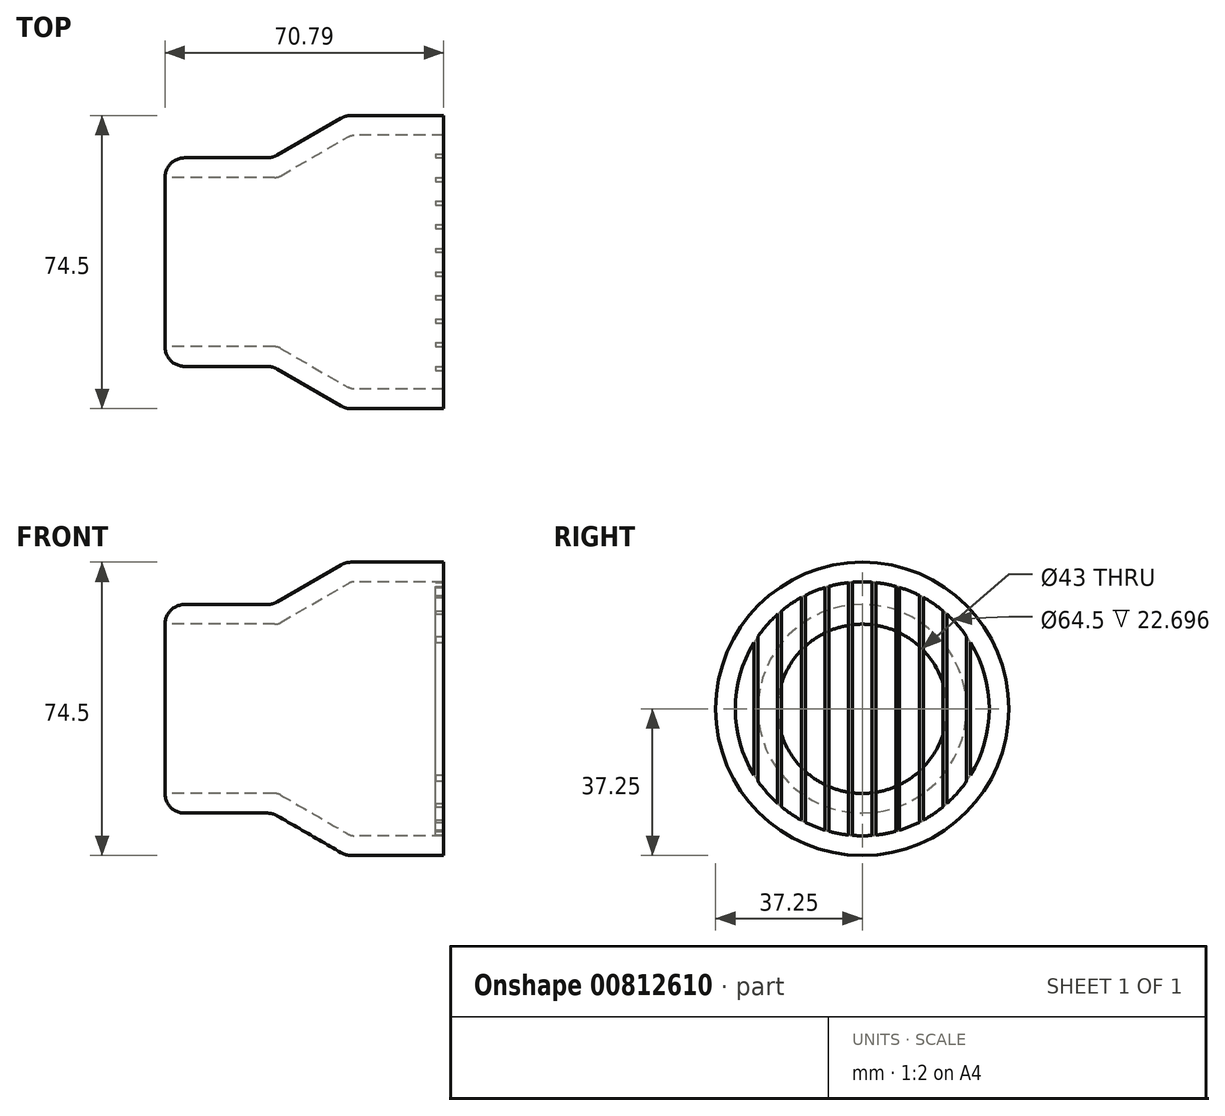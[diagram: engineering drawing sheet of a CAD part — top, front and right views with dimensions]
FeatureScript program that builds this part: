
annotation { "Feature Type Name" : "Feature", "Feature Type Description" : "" }
export const myFeature = defineFeature(function(context is Context, id is Id, definition is map)
    precondition{}
    {
        {
            var Q0;
            Q0=qCreatedBy(makeId("Top.planeOp"),FACE);
            var sketch = newSketch(context, id + "F0", { "sketchPlane" : qUnion([Q0])});
            skLineSegment(sketch, "E0", {"start": v(-28.67, 21.5) * mm, "end": v(0, 21.5) * mm});
            skLineSegment(sketch, "E1", {"start": v(0, 21.5) * mm, "end": v(18.62, 32.25) * mm});
            skLineSegment(sketch, "E2", {"start": v(18.62, 32.25) * mm, "end": v(40.12, 32.25) * mm});
            skLineSegment(sketch, "E3.0", {"start": v(17.28, 37.25) * mm, "end": v(40.12, 37.25) * mm});
            skLineSegment(sketch, "E3.1", {"start": v(-1.34, 26.5) * mm, "end": v(17.28, 37.25) * mm});
            skLineSegment(sketch, "E3.2", {"start": v(-28.67, 26.5) * mm, "end": v(-1.34, 26.5) * mm});
            skLineSegment(sketch, "E4", {"start": v(-28.67, 21.5) * mm, "end": v(-28.67, 26.5) * mm});
            skLineSegment(sketch, "E5", {"start": v(40.12, 37.25) * mm, "end": v(40.12, 32.25) * mm});
            skLineSegment(sketch, "E6", {"start": v(-63.57, 0) * mm, "end": v(46.05, 0) * mm});
            skSolve(sketch);
        }
        {
            var Q0;
            Q0=qSketchRegion(id+"F0",true);
            var Q1;
            Q1=sQuery(id+"F0.wireOp",EDGE,"E6");
            revolve(context, id + "F1", {"surfaceOperationType" : NewSurfaceOperationType.NEW, "entities" : qUnion([Q0]), "axis" : qUnion([Q1]), "revolveType" : RevolveType.FULL});
        }
        {
            var Q0;
            Q0=makeQuery(id+"F1.opRevolve","SWEPT_FACE",FACE,{"disambiguationData":[OSD([sQuery(id+"F0.wireOp",EDGE,"E5")])]});
            var sketch = newSketch(context, id + "F2", { "sketchPlane" : qUnion([Q0])});
            skCircle(sketch, "E7.0", {"center": v(0, 0) * mm, "radius": 37.25 * mm});
            skSolve(sketch);
        }
        {
            var Q0;
            Q0=qSketchRegion(id+"F2",true);
            extrude(context, id + "F3", {"entities" : qUnion([Q0]), "operationType" : NewBodyOperationType.ADD, "depth" : 2 * mm, "offsetDistance" : 25 * mm});
        }
        {
            var Q0;
            Q0=makeQuery(id+"F3.opExtrude","CAP_FACE",FACE,{"disambiguationData":[OSD([sQuery(id+"F2.wireOp",EDGE,"E7.0")])],"isStart":false});
            var sketch = newSketch(context, id + "F4", { "sketchPlane" : qUnion([Q0])});
            skLineSegment(sketch, "E8.bottom", {"start": v(-2.5, 42.44) * mm, "end": v(2.5, 42.44) * mm});
            skLineSegment(sketch, "E8.top", {"start": v(-2.5, -43.56) * mm, "end": v(2.5, -43.56) * mm});
            skLineSegment(sketch, "E8.left", {"start": v(-2.5, 42.44) * mm, "end": v(-2.5, -43.56) * mm});
            skLineSegment(sketch, "E8.right", {"start": v(2.5, 42.44) * mm, "end": v(2.5, -43.56) * mm});
            skLineSegment(sketch, "E9.1.0.0", {"start": v(3.5, -43.56) * mm, "end": v(8.5, -43.56) * mm});
            skLineSegment(sketch, "E9.1.0.1", {"start": v(8.5, 42.44) * mm, "end": v(8.5, -43.56) * mm});
            skLineSegment(sketch, "E9.1.0.2", {"start": v(3.5, 42.44) * mm, "end": v(3.5, -43.56) * mm});
            skLineSegment(sketch, "E9.1.0.3", {"start": v(3.5, 42.44) * mm, "end": v(8.5, 42.44) * mm});
            skLineSegment(sketch, "E9.2.0.0", {"start": v(9.5, -43.56) * mm, "end": v(14.5, -43.56) * mm});
            skLineSegment(sketch, "E9.2.0.1", {"start": v(14.5, 42.44) * mm, "end": v(14.5, -43.56) * mm});
            skLineSegment(sketch, "E9.2.0.2", {"start": v(9.5, 42.44) * mm, "end": v(9.5, -43.56) * mm});
            skLineSegment(sketch, "E9.2.0.3", {"start": v(9.5, 42.44) * mm, "end": v(14.5, 42.44) * mm});
            skLineSegment(sketch, "E9.3.0.0", {"start": v(15.5, -43.56) * mm, "end": v(20.5, -43.56) * mm});
            skLineSegment(sketch, "E9.3.0.1", {"start": v(20.5, 42.44) * mm, "end": v(20.5, -43.56) * mm});
            skLineSegment(sketch, "E9.3.0.2", {"start": v(15.5, 42.44) * mm, "end": v(15.5, -43.56) * mm});
            skLineSegment(sketch, "E9.3.0.3", {"start": v(15.5, 42.44) * mm, "end": v(20.5, 42.44) * mm});
            skLineSegment(sketch, "E9.4.0.0", {"start": v(21.5, -43.56) * mm, "end": v(26.5, -43.56) * mm});
            skLineSegment(sketch, "E9.4.0.1", {"start": v(26.5, 42.44) * mm, "end": v(26.5, -43.56) * mm});
            skLineSegment(sketch, "E9.4.0.2", {"start": v(21.5, 42.44) * mm, "end": v(21.5, -43.56) * mm});
            skLineSegment(sketch, "E9.4.0.3", {"start": v(21.5, 42.44) * mm, "end": v(26.5, 42.44) * mm});
            skLineSegment(sketch, "E9.5.0.0", {"start": v(27.5, -43.56) * mm, "end": v(32.5, -43.56) * mm});
            skLineSegment(sketch, "E9.5.0.1", {"start": v(32.5, 42.44) * mm, "end": v(32.5, -43.56) * mm});
            skLineSegment(sketch, "E9.5.0.2", {"start": v(27.5, 42.44) * mm, "end": v(27.5, -43.56) * mm});
            skLineSegment(sketch, "E9.5.0.3", {"start": v(27.5, 42.44) * mm, "end": v(32.5, 42.44) * mm});
            skLineSegment(sketch, "E9.direction1", {"start": v(-2.5, -43.56) * mm, "end": v(3.5, -43.56) * mm, "construction": true});
            skLineSegment(sketch, "E10.1.0.0", {"start": v(-3.5, 42.44) * mm, "end": v(-3.5, -43.56) * mm});
            skLineSegment(sketch, "E10.1.0.1", {"start": v(-8.5, -43.56) * mm, "end": v(-3.5, -43.56) * mm});
            skLineSegment(sketch, "E10.1.0.2", {"start": v(-8.5, 42.44) * mm, "end": v(-8.5, -43.56) * mm});
            skLineSegment(sketch, "E10.1.0.3", {"start": v(-8.5, 42.44) * mm, "end": v(-3.5, 42.44) * mm});
            skLineSegment(sketch, "E10.2.0.0", {"start": v(-9.5, 42.44) * mm, "end": v(-9.5, -43.56) * mm});
            skLineSegment(sketch, "E10.2.0.1", {"start": v(-14.5, -43.56) * mm, "end": v(-9.5, -43.56) * mm});
            skLineSegment(sketch, "E10.2.0.2", {"start": v(-14.5, 42.44) * mm, "end": v(-14.5, -43.56) * mm});
            skLineSegment(sketch, "E10.2.0.3", {"start": v(-14.5, 42.44) * mm, "end": v(-9.5, 42.44) * mm});
            skLineSegment(sketch, "E10.3.0.0", {"start": v(-15.5, 42.44) * mm, "end": v(-15.5, -43.56) * mm});
            skLineSegment(sketch, "E10.3.0.1", {"start": v(-20.5, -43.56) * mm, "end": v(-15.5, -43.56) * mm});
            skLineSegment(sketch, "E10.3.0.2", {"start": v(-20.5, 42.44) * mm, "end": v(-20.5, -43.56) * mm});
            skLineSegment(sketch, "E10.3.0.3", {"start": v(-20.5, 42.44) * mm, "end": v(-15.5, 42.44) * mm});
            skLineSegment(sketch, "E10.4.0.0", {"start": v(-21.5, 42.44) * mm, "end": v(-21.5, -43.56) * mm});
            skLineSegment(sketch, "E10.4.0.1", {"start": v(-26.5, -43.56) * mm, "end": v(-21.5, -43.56) * mm});
            skLineSegment(sketch, "E10.4.0.2", {"start": v(-26.5, 42.44) * mm, "end": v(-26.5, -43.56) * mm});
            skLineSegment(sketch, "E10.4.0.3", {"start": v(-26.5, 42.44) * mm, "end": v(-21.5, 42.44) * mm});
            skLineSegment(sketch, "E10.5.0.0", {"start": v(-27.5, 42.44) * mm, "end": v(-27.5, -43.56) * mm});
            skLineSegment(sketch, "E10.5.0.1", {"start": v(-32.5, -43.56) * mm, "end": v(-27.5, -43.56) * mm});
            skLineSegment(sketch, "E10.5.0.2", {"start": v(-32.5, 42.44) * mm, "end": v(-32.5, -43.56) * mm});
            skLineSegment(sketch, "E10.5.0.3", {"start": v(-32.5, 42.44) * mm, "end": v(-27.5, 42.44) * mm});
            skLineSegment(sketch, "E10.direction1", {"start": v(-2.5, -43.56) * mm, "end": v(-8.5, -43.56) * mm, "construction": true});
            skCircle(sketch, "E11.0", {"center": v(0, 0) * mm, "radius": 37.25 * mm});
            skCircle(sketch, "E12", {"center": v(0, 0) * mm, "radius": 32.25 * mm});
            skSolve(sketch);
        }
        {
            var Q0;
            {var subQ0=sQuery(id+"F4.wireOp",EDGE,"E12");var subQ1=sQuery(id+"F4.wireOp",EDGE,"E9.5.0.2");var subQ2=makeQuery(id+"F4.imprint","INTERSECT",VERTEX,{"disambiguationData":[OD(0.0)],"derivedFrom":[subQ1,subQ0]});Q0=makeQuery(id+"F4.imprint","IMPRINT",FACE,{"disambiguationData":[TD([[makeQuery(id+"F4.imprint","IMPRINT",EDGE,{"disambiguationData":[TD([[subQ2,-1.0]])],"derivedFrom":subQ1}),1.0]])]});}
            var Q1;
            {var subQ0=sQuery(id+"F4.wireOp",EDGE,"E12");var subQ1=sQuery(id+"F4.wireOp",EDGE,"E9.4.0.1");var subQ2=makeQuery(id+"F4.imprint","INTERSECT",VERTEX,{"disambiguationData":[OD(0.0)],"derivedFrom":[subQ1,subQ0]});Q1=makeQuery(id+"F4.imprint","IMPRINT",FACE,{"disambiguationData":[TD([[makeQuery(id+"F4.imprint","IMPRINT",EDGE,{"disambiguationData":[TD([[subQ2,-1.0]])],"derivedFrom":subQ1}),-1.0]])]});}
            var Q2;
            {var subQ0=sQuery(id+"F4.wireOp",EDGE,"E12");var subQ1=sQuery(id+"F4.wireOp",EDGE,"E9.3.0.1");var subQ2=makeQuery(id+"F4.imprint","INTERSECT",VERTEX,{"disambiguationData":[OD(0.0)],"derivedFrom":[subQ1,subQ0]});Q2=makeQuery(id+"F4.imprint","IMPRINT",FACE,{"disambiguationData":[TD([[makeQuery(id+"F4.imprint","IMPRINT",EDGE,{"disambiguationData":[TD([[subQ2,-1.0]])],"derivedFrom":subQ1}),-1.0]])]});}
            var Q3;
            {var subQ0=sQuery(id+"F4.wireOp",EDGE,"E12");var subQ1=sQuery(id+"F4.wireOp",EDGE,"E9.2.0.1");var subQ2=makeQuery(id+"F4.imprint","INTERSECT",VERTEX,{"disambiguationData":[OD(0.0)],"derivedFrom":[subQ1,subQ0]});Q3=makeQuery(id+"F4.imprint","IMPRINT",FACE,{"disambiguationData":[TD([[makeQuery(id+"F4.imprint","IMPRINT",EDGE,{"disambiguationData":[TD([[subQ2,-1.0]])],"derivedFrom":subQ1}),-1.0]])]});}
            var Q4;
            {var subQ0=sQuery(id+"F4.wireOp",EDGE,"E12");var subQ1=sQuery(id+"F4.wireOp",EDGE,"E9.1.0.1");var subQ2=makeQuery(id+"F4.imprint","INTERSECT",VERTEX,{"disambiguationData":[OD(0.0)],"derivedFrom":[subQ1,subQ0]});Q4=makeQuery(id+"F4.imprint","IMPRINT",FACE,{"disambiguationData":[TD([[makeQuery(id+"F4.imprint","IMPRINT",EDGE,{"disambiguationData":[TD([[subQ2,-1.0]])],"derivedFrom":subQ1}),-1.0]])]});}
            var Q5;
            {var subQ0=sQuery(id+"F4.wireOp",EDGE,"E12");var subQ1=sQuery(id+"F4.wireOp",EDGE,"E8.left");var subQ2=makeQuery(id+"F4.imprint","INTERSECT",VERTEX,{"disambiguationData":[OD(0.0)],"derivedFrom":[subQ1,subQ0]});Q5=makeQuery(id+"F4.imprint","IMPRINT",FACE,{"disambiguationData":[TD([[makeQuery(id+"F4.imprint","IMPRINT",EDGE,{"disambiguationData":[TD([[subQ2,-1.0]])],"derivedFrom":subQ1}),1.0]])]});}
            var Q6;
            {var subQ0=sQuery(id+"F4.wireOp",EDGE,"E12");var subQ1=sQuery(id+"F4.wireOp",EDGE,"E10.1.0.0");var subQ2=makeQuery(id+"F4.imprint","INTERSECT",VERTEX,{"disambiguationData":[OD(0.0)],"derivedFrom":[subQ1,subQ0]});Q6=makeQuery(id+"F4.imprint","IMPRINT",FACE,{"disambiguationData":[TD([[makeQuery(id+"F4.imprint","IMPRINT",EDGE,{"disambiguationData":[TD([[subQ2,-1.0]])],"derivedFrom":subQ1}),-1.0]])]});}
            var Q7;
            {var subQ0=sQuery(id+"F4.wireOp",EDGE,"E12");var subQ1=sQuery(id+"F4.wireOp",EDGE,"E10.2.0.0");var subQ2=makeQuery(id+"F4.imprint","INTERSECT",VERTEX,{"disambiguationData":[OD(0.0)],"derivedFrom":[subQ1,subQ0]});Q7=makeQuery(id+"F4.imprint","IMPRINT",FACE,{"disambiguationData":[TD([[makeQuery(id+"F4.imprint","IMPRINT",EDGE,{"disambiguationData":[TD([[subQ2,-1.0]])],"derivedFrom":subQ1}),-1.0]])]});}
            var Q8;
            {var subQ0=sQuery(id+"F4.wireOp",EDGE,"E12");var subQ1=sQuery(id+"F4.wireOp",EDGE,"E10.3.0.0");var subQ2=makeQuery(id+"F4.imprint","INTERSECT",VERTEX,{"disambiguationData":[OD(0.0)],"derivedFrom":[subQ1,subQ0]});Q8=makeQuery(id+"F4.imprint","IMPRINT",FACE,{"disambiguationData":[TD([[makeQuery(id+"F4.imprint","IMPRINT",EDGE,{"disambiguationData":[TD([[subQ2,-1.0]])],"derivedFrom":subQ1}),-1.0]])]});}
            var Q9;
            {var subQ0=sQuery(id+"F4.wireOp",EDGE,"E12");var subQ1=sQuery(id+"F4.wireOp",EDGE,"E10.4.0.0");var subQ2=makeQuery(id+"F4.imprint","INTERSECT",VERTEX,{"disambiguationData":[OD(0.0)],"derivedFrom":[subQ1,subQ0]});Q9=makeQuery(id+"F4.imprint","IMPRINT",FACE,{"disambiguationData":[TD([[makeQuery(id+"F4.imprint","IMPRINT",EDGE,{"disambiguationData":[TD([[subQ2,-1.0]])],"derivedFrom":subQ1}),-1.0]])]});}
            var Q10;
            {var subQ0=sQuery(id+"F4.wireOp",EDGE,"E12");var subQ1=sQuery(id+"F4.wireOp",EDGE,"E10.5.0.0");var subQ2=makeQuery(id+"F4.imprint","INTERSECT",VERTEX,{"disambiguationData":[OD(0.0)],"derivedFrom":[subQ1,subQ0]});Q10=makeQuery(id+"F4.imprint","IMPRINT",FACE,{"disambiguationData":[TD([[makeQuery(id+"F4.imprint","IMPRINT",EDGE,{"disambiguationData":[TD([[subQ2,-1.0]])],"derivedFrom":subQ1}),-1.0]])]});}
            var Q11;
            Q11=makeQuery(id+"F3.opExtrude","CAP_FACE",FACE,{"disambiguationData":[OSD([sQuery(id+"F2.wireOp",EDGE,"E7.0")])],"isStart":true});
            extrude(context, id + "F5", {"entities" : qUnion([Q0, Q1, Q2, Q3, Q4, Q5, Q6, Q7, Q8, Q9, Q10]), "operationType" : NewBodyOperationType.REMOVE, "endBound" : BoundingType.UP_TO_SURFACE, "oppositeDirection" : true, "depth" : 25 * mm, "endBoundEntityFace" : qUnion([Q11]), "offsetDistance" : 25 * mm});
        }
        {
            var Q0;
            Q0=makeQuery(id+"F1.opRevolve","SWEPT_EDGE",EDGE,{"disambiguationData":[OSD([sQuery(id+"F0.wireOp",EDGE,"E3.2"),sQuery(id+"F0.wireOp",EDGE,"E4")])]});
            var Q1;
            Q1=makeQuery(id+"F1.opRevolve","SWEPT_EDGE",EDGE,{"disambiguationData":[OSD([sQuery(id+"F0.wireOp",EDGE,"E3.1"),sQuery(id+"F0.wireOp",EDGE,"E3.2")])]});
            var Q2;
            Q2=makeQuery(id+"F1.opRevolve","SWEPT_EDGE",EDGE,{"disambiguationData":[OSD([sQuery(id+"F0.wireOp",EDGE,"E3.0"),sQuery(id+"F0.wireOp",EDGE,"E3.1")])]});
            fillet(context, id + "F6", {"entities" : qUnion([Q0, Q1, Q2]), "radius" : 5 * mm, "tangentPropagation" : true, "allowEdgeOverflow" : false});
        }
        {
            var Q0;
            Q0=makeQuery(id+"F1.opRevolve","SWEPT_EDGE",EDGE,{"disambiguationData":[OSD([sQuery(id+"F0.wireOp",EDGE,"E1"),sQuery(id+"F0.wireOp",EDGE,"E2")])]});
            var Q1;
            Q1=makeQuery(id+"F1.opRevolve","SWEPT_EDGE",EDGE,{"disambiguationData":[OSD([sQuery(id+"F0.wireOp",EDGE,"E0"),sQuery(id+"F0.wireOp",EDGE,"E1")])]});
            fillet(context, id + "F7", {"entities" : qUnion([Q0, Q1]), "radius" : 3 * mm, "tangentPropagation" : true, "allowEdgeOverflow" : false});
        }
    });
